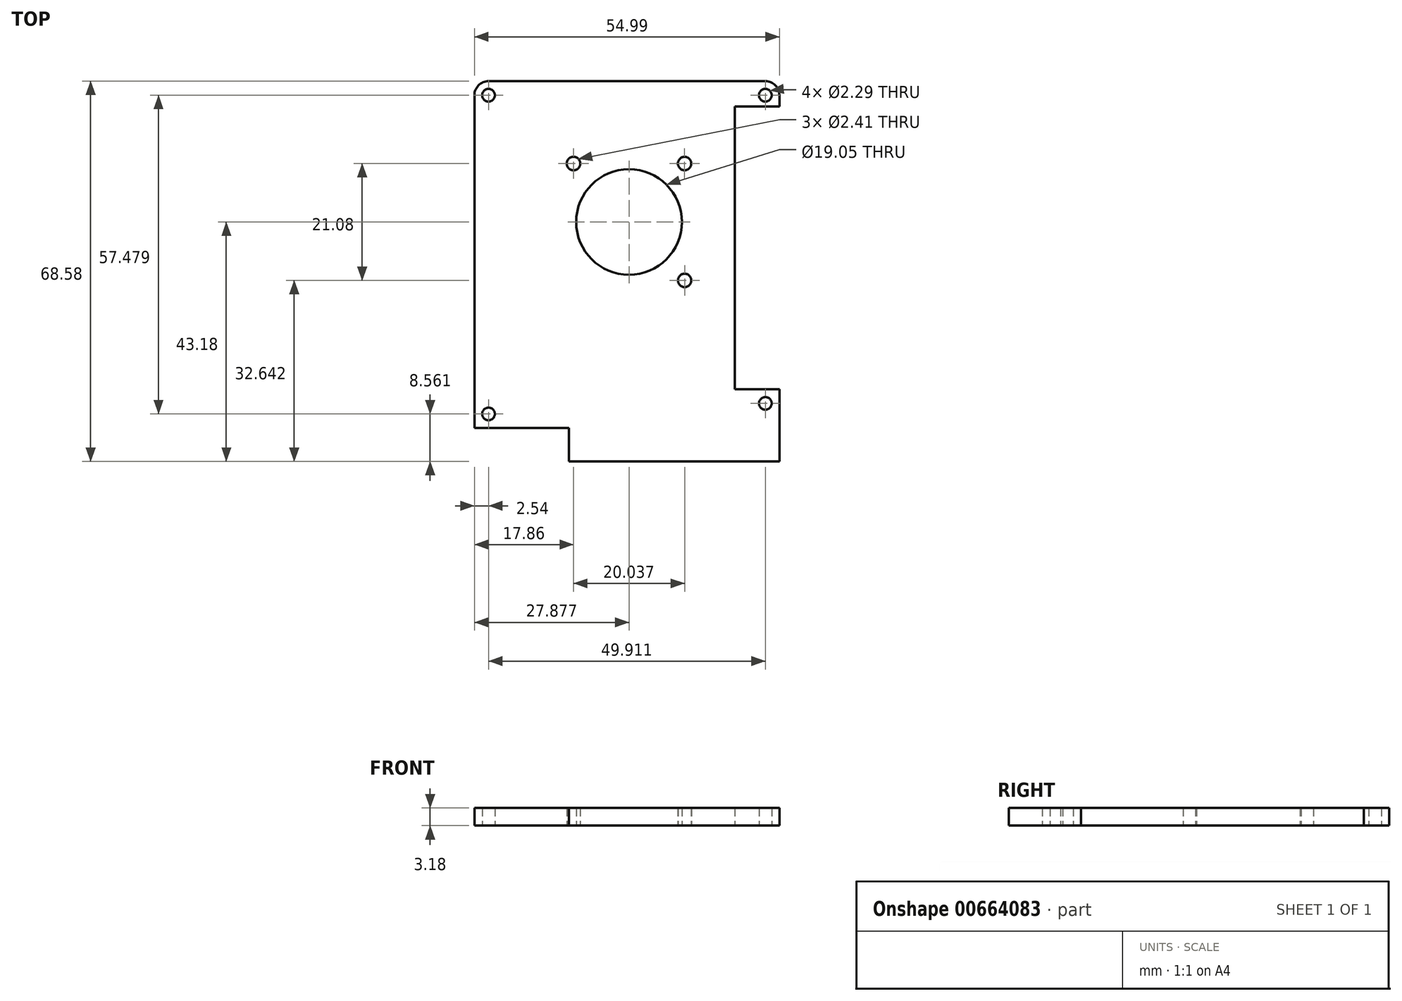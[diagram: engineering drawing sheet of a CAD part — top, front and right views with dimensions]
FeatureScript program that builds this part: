
annotation { "Feature Type Name" : "Feature", "Feature Type Description" : "" }
export const myFeature = defineFeature(function(context is Context, id is Id, definition is map)
    precondition{}
    {
        {
            var Q0;
            Q0=qCreatedBy(makeId("Top.planeOp"),FACE);
            var sketch = newSketch(context, id + "F0", { "sketchPlane" : qUnion([Q0])});
            skLineSegment(sketch, "E0.bottom", {"start": v(2.54, 0) * mm, "end": v(52.45, 0) * mm});
            skLineSegment(sketch, "E0.top", {"start": v(17.04, -68.58) * mm, "end": v(55, -68.58) * mm});
            skLineSegment(sketch, "E0.left", {"start": v(0, -2.54) * mm, "end": v(0, -62.56) * mm});
            skLineSegment(sketch, "E0.right", {"start": v(55, -2.54) * mm, "end": v(55, -68.58) * mm});
            skLineSegment(sketch, "E1", {"start": v(55, -68.58) * mm, "end": v(17.04, -68.58) * mm});
            skLineSegment(sketch, "E2", {"start": v(17.04, -68.58) * mm, "end": v(17.04, -62.56) * mm});
            skLineSegment(sketch, "E3", {"start": v(17.04, -62.56) * mm, "end": v(0, -62.56) * mm});
            skPoint(sketch, "E4.visualSharp", {"position": v(0, 0) * mm});
            skArc(sketch, "E4.filletArc", {"start": v(2.54, 0) * mm, "mid": v(0.74, -0.74) * mm, "end": v(0, -2.54) * mm});
            skPoint(sketch, "E5.visualSharp", {"position": v(55, 0) * mm});
            skArc(sketch, "E5.filletArc", {"start": v(55, -2.54) * mm, "mid": v(54.25, -0.74) * mm, "end": v(52.45, 0) * mm});
            skLineSegment(sketch, "E6", {"start": v(55, 0) * mm, "end": v(55, -4.58) * mm});
            skLineSegment(sketch, "E7", {"start": v(55, -4.58) * mm, "end": v(46.93, -4.58) * mm});
            skLineSegment(sketch, "E8", {"start": v(46.93, -4.58) * mm, "end": v(46.93, -55.58) * mm});
            skLineSegment(sketch, "E9", {"start": v(46.93, -55.58) * mm, "end": v(55, -55.58) * mm});
            skLineSegment(sketch, "E10", {"start": v(55, -55.58) * mm, "end": v(55, -68.58) * mm});
            skCircle(sketch, "E11", {"center": v(27.88, -25.4) * mm, "radius": 9.53 * mm});
            skCircle(sketch, "E12", {"center": v(2.54, -2.54) * mm, "radius": 1.14 * mm});
            skCircle(sketch, "E13", {"center": v(52.45, -2.54) * mm, "radius": 1.14 * mm});
            skCircle(sketch, "E14", {"center": v(2.54, -60.02) * mm, "radius": 1.14 * mm});
            skCircle(sketch, "E15", {"center": v(52.45, -58.12) * mm, "radius": 1.14 * mm});
            skCircle(sketch, "E16", {"center": v(17.86, -14.86) * mm, "radius": 1.2 * mm});
            skCircle(sketch, "E17", {"center": v(37.9, -14.86) * mm, "radius": 1.2 * mm});
            skCircle(sketch, "E18", {"center": v(37.9, -35.94) * mm, "radius": 1.2 * mm});
            skLineSegment(sketch, "E19", {"start": v(17.86, -14.86) * mm, "end": v(37.9, -14.86) * mm, "construction": true});
            skLineSegment(sketch, "E20", {"start": v(37.9, -14.86) * mm, "end": v(37.9, -35.94) * mm, "construction": true});
            skSolve(sketch);
        }
        {
            var Q0;
            Q0=makeQuery(id+"F0.imprint","IMPRINT",FACE,{"disambiguationData":[TD([[makeQuery(id+"F0.imprint","IMPRINT",EDGE,{"derivedFrom":sQuery(id+"F0.wireOp",EDGE,"E0.bottom")}),-1.0]])]});
            extrude(context, id + "F1", {"entities" : qUnion([Q0]), "depth" : 3.17 * mm, "offsetDistance" : 25.4 * mm});
        }
    });
